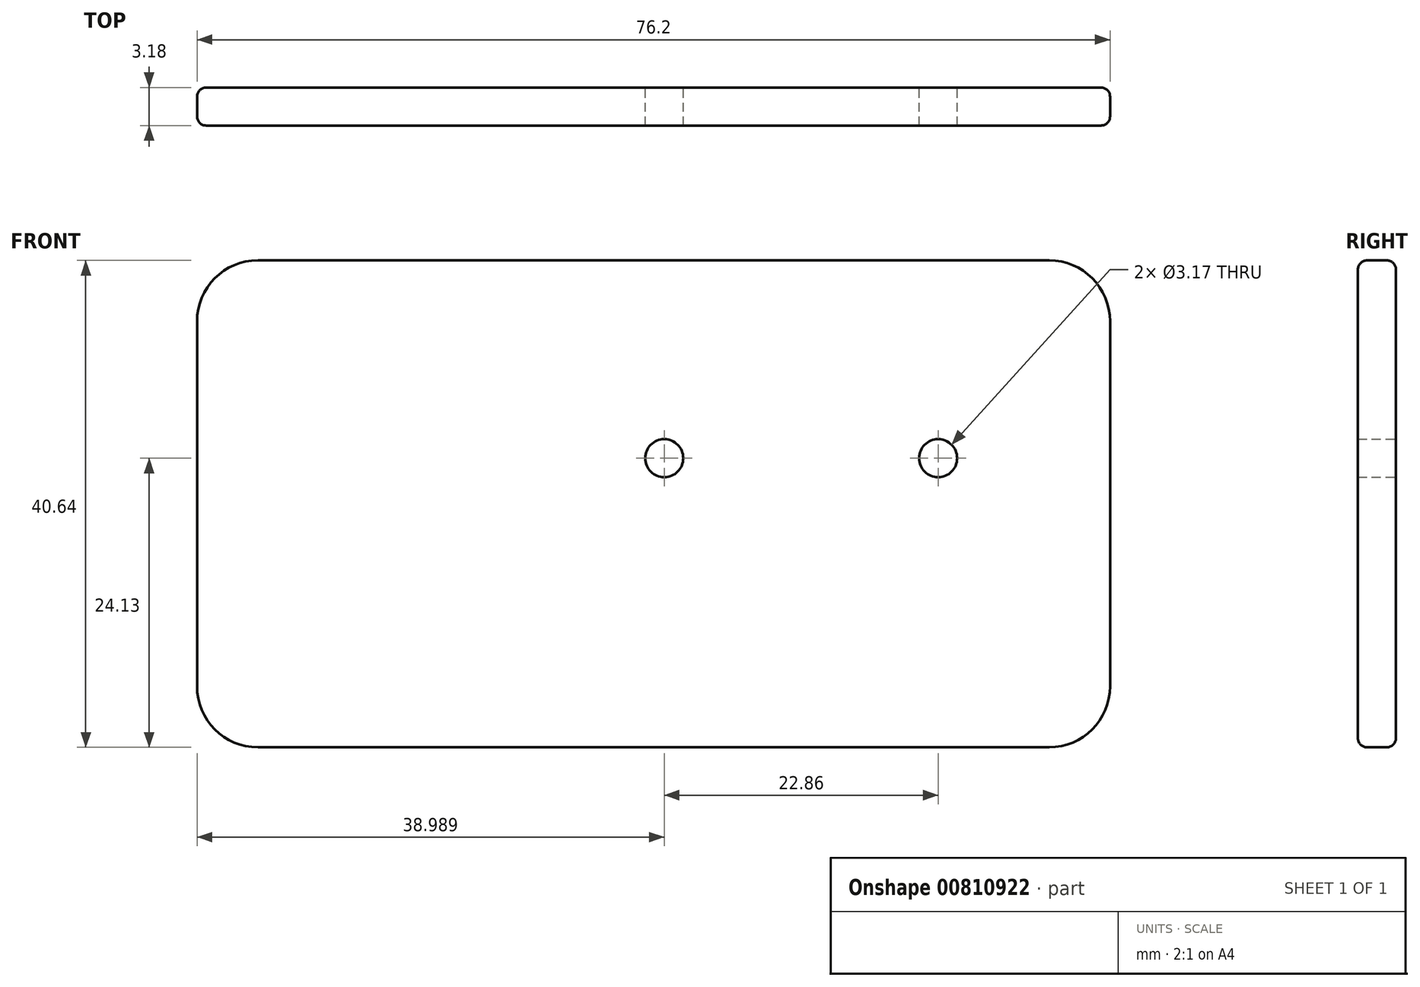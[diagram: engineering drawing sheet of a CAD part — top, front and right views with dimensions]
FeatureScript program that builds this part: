
annotation { "Feature Type Name" : "Feature", "Feature Type Description" : "" }
export const myFeature = defineFeature(function(context is Context, id is Id, definition is map)
    precondition{}
    {
        {
            var Q0;
            Q0=qCreatedBy(makeId("Front.planeOp"),FACE);
            var sketch = newSketch(context, id + "F0", { "sketchPlane" : qUnion([Q0])});
            skLineSegment(sketch, "E0.bottom", {"start": v(33.02, -24.13) * mm, "end": v(-43.18, -24.13) * mm});
            skLineSegment(sketch, "E0.right", {"start": v(-43.18, -24.13) * mm, "end": v(-43.18, 16.51) * mm});
            skPoint(sketch, "E0.middle", {"position": v(0, 0) * mm});
            skCircle(sketch, "E1", {"center": v(-4.2, 0) * mm, "radius": 1.59 * mm});
            skCircle(sketch, "E2", {"center": v(18.67, 0) * mm, "radius": 1.59 * mm});
            skLineSegment(sketch, "E3", {"start": v(-43.18, 16.51) * mm, "end": v(33.02, 16.51) * mm});
            skLineSegment(sketch, "E4", {"start": v(33.02, -24.13) * mm, "end": v(33.02, 16.51) * mm});
            skPoint(sketch, "E5.orphan", {"position": v(43.18, 24.13) * mm});
            skPoint(sketch, "E0.left.start.orphan", {"position": v(43.18, -24.13) * mm});
            skPoint(sketch, "E6.orphan", {"position": v(-43.18, 24.13) * mm});
            skSolve(sketch);
        }
        {
            var Q0;
            Q0=makeQuery(id+"F0.imprint","IMPRINT",FACE,{"disambiguationData":[TD([[makeQuery(id+"F0.imprint","IMPRINT",EDGE,{"derivedFrom":sQuery(id+"F0.wireOp",EDGE,"E0.bottom")}),-1.0]])]});
            extrude(context, id + "F1", {"entities" : qUnion([Q0]), "depth" : 3.17 * mm, "offsetDistance" : 25.4 * mm});
        }
        {
            var Q0;
            Q0=makeQuery(id+"F1.opExtrude","SWEPT_EDGE",EDGE,{"disambiguationData":[OSD([sQuery(id+"F0.wireOp",EDGE,"E0.top"),sQuery(id+"F0.wireOp",EDGE,"E0.left")])]});
            var Q1;
            Q1=makeQuery(id+"F1.opExtrude","SWEPT_EDGE",EDGE,{"disambiguationData":[OSD([sQuery(id+"F0.wireOp",EDGE,"E0.top"),sQuery(id+"F0.wireOp",EDGE,"E0.right")])]});
            var Q2;
            Q2=makeQuery(id+"F1.opExtrude","SWEPT_EDGE",EDGE,{"disambiguationData":[OSD([sQuery(id+"F0.wireOp",EDGE,"E0.bottom"),sQuery(id+"F0.wireOp",EDGE,"E0.right")])]});
            var Q3;
            Q3=makeQuery(id+"F1.opExtrude","SWEPT_EDGE",EDGE,{"disambiguationData":[OSD([sQuery(id+"F0.wireOp",EDGE,"E0.bottom"),sQuery(id+"F0.wireOp",EDGE,"E0.left")])]});
            var Q4;
            Q4=makeQuery(id+"F1.opExtrude","SWEPT_EDGE",EDGE,{"disambiguationData":[OSD([sQuery(id+"F0.wireOp",EDGE,"E3"),sQuery(id+"F0.wireOp",EDGE,"E4")])]});
            fillet(context, id + "F2", {"entities" : qUnion([Q0, Q1, Q2, Q3, Q4]), "radius" : 5.08 * mm, "tangentPropagation" : true, "allowEdgeOverflow" : false});
        }
        {
            var Q0;
            Q0=makeQuery(id+"F1.opExtrude","CAP_EDGE",EDGE,{"disambiguationData":[OSD([sQuery(id+"F0.wireOp",EDGE,"E0.bottom")])],"isStart":true});
            var Q1;
            Q1=makeQuery(id+"F1.opExtrude","CAP_EDGE",EDGE,{"disambiguationData":[OSD([sQuery(id+"F0.wireOp",EDGE,"E0.bottom")])],"isStart":false});
            var Q2;
            Q2=makeQuery(id+"F1.opExtrude","CAP_EDGE",EDGE,{"disambiguationData":[OSD([sQuery(id+"F0.wireOp",EDGE,"E0.left")])],"isStart":false});
            var Q3;
            Q3=makeQuery(id+"F1.opExtrude","CAP_EDGE",EDGE,{"disambiguationData":[OSD([sQuery(id+"F0.wireOp",EDGE,"E0.left")])],"isStart":true});
            var Q4;
            Q4=makeQuery(id+"F1.opExtrude","CAP_EDGE",EDGE,{"disambiguationData":[OSD([sQuery(id+"F0.wireOp",EDGE,"E0.right")])],"isStart":false});
            var Q5;
            Q5=makeQuery(id+"F1.opExtrude","CAP_EDGE",EDGE,{"disambiguationData":[OSD([sQuery(id+"F0.wireOp",EDGE,"E0.right")])],"isStart":true});
            var Q6;
            Q6=makeQuery(id+"F1.opExtrude","CAP_EDGE",EDGE,{"disambiguationData":[OSD([sQuery(id+"F0.wireOp",EDGE,"E0.top")])],"isStart":false});
            var Q7;
            Q7=makeQuery(id+"F1.opExtrude","CAP_EDGE",EDGE,{"disambiguationData":[OSD([sQuery(id+"F0.wireOp",EDGE,"E0.top")])],"isStart":true});
            fillet(context, id + "F3", {"entities" : qUnion([Q0, Q1, Q2, Q3, Q4, Q5, Q6, Q7]), "radius" : 0.76 * mm, "tangentPropagation" : true, "allowEdgeOverflow" : false});
        }
    });
